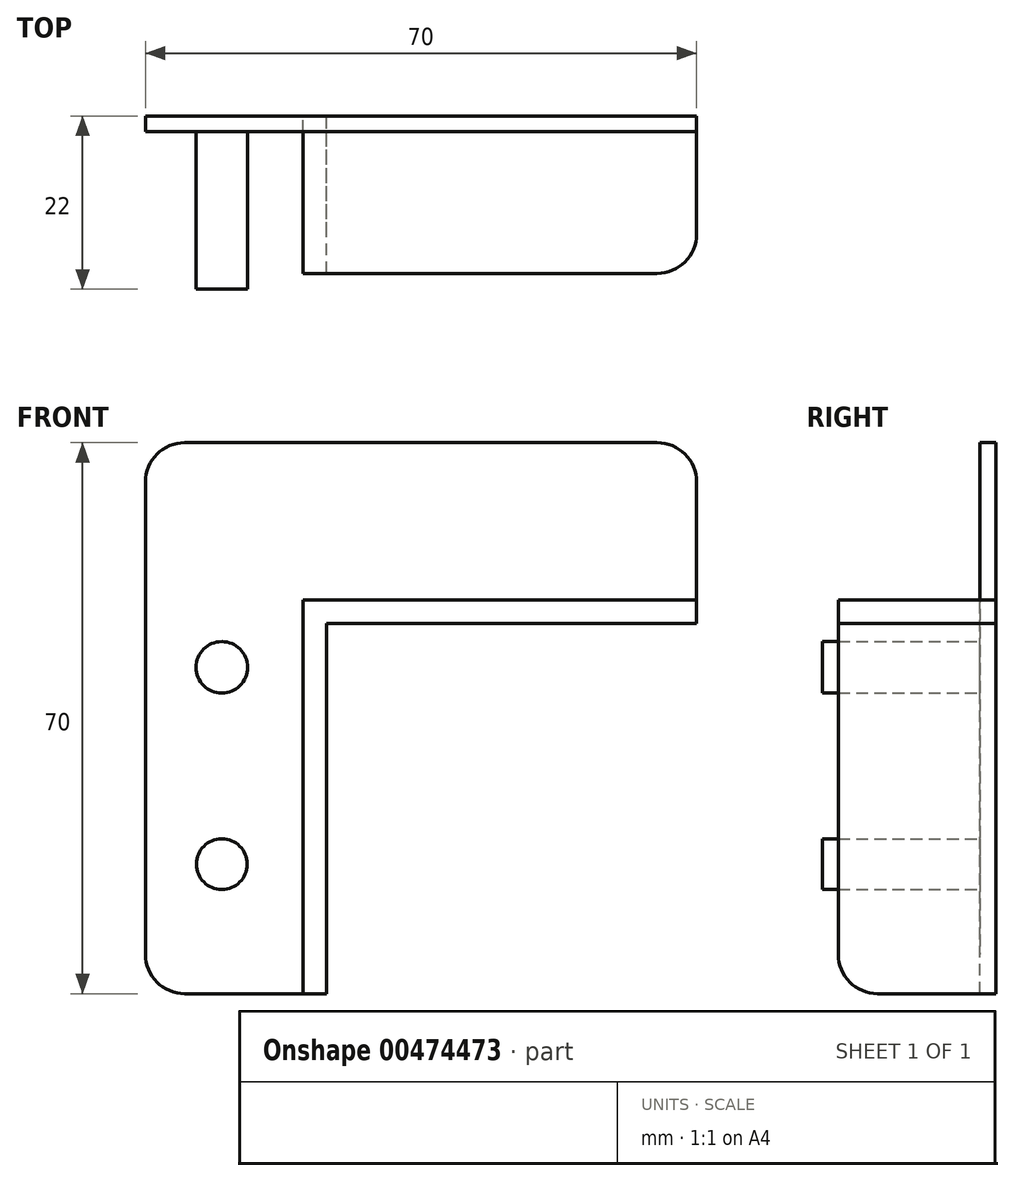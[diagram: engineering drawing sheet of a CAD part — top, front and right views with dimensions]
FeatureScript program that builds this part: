
annotation { "Feature Type Name" : "Feature", "Feature Type Description" : "" }
export const myFeature = defineFeature(function(context is Context, id is Id, definition is map)
    precondition{}
    {
        {
            var Q0;
            Q0=qCreatedBy(makeId("Front.planeOp"),FACE);
            var sketch = newSketch(context, id + "F0", { "sketchPlane" : qUnion([Q0])});
            skLineSegment(sketch, "E0.top", {"start": v(25, 25) * mm, "end": v(-25, 25) * mm});
            skLineSegment(sketch, "E0.right", {"start": v(-25, -25) * mm, "end": v(-25, 25) * mm});
            skPoint(sketch, "E0.middle", {"position": v(0, 0) * mm});
            skLineSegment(sketch, "E1.top", {"start": v(22, 22) * mm, "end": v(-22, 22) * mm});
            skLineSegment(sketch, "E1.right", {"start": v(-22, -22) * mm, "end": v(-22, 22) * mm});
            skLineSegment(sketch, "E2", {"start": v(22, 22) * mm, "end": v(25, 22) * mm});
            skLineSegment(sketch, "E3", {"start": v(-22, -22) * mm, "end": v(-22, -25) * mm});
            skLineSegment(sketch, "E4", {"start": v(-25, -25) * mm, "end": v(-22, -25) * mm});
            skLineSegment(sketch, "E5", {"start": v(25, 25) * mm, "end": v(25, 22) * mm});
            skSolve(sketch);
        }
        {
            var Q0;
            Q0 = qSketchRegion(id + "F0", true);
            extrude(context, id + "F1", {"entities" : qUnion([Q0]), "endBound" : BoundingType.SYMMETRIC, "depth" : 20 * mm});
        }
        {
            var Q0;
            Q0=makeQuery(id+"F1.opExtrude","CAP_FACE",FACE,{"disambiguationData":[OSD([sQuery(id+"F0.wireOp",EDGE,"E0.top"),sQuery(id+"F0.wireOp",EDGE,"E0.right"),sQuery(id+"F0.wireOp",EDGE,"E1.top"),sQuery(id+"F0.wireOp",EDGE,"E1.right"),sQuery(id+"F0.wireOp",EDGE,"E2"),sQuery(id+"F0.wireOp",EDGE,"E3"),sQuery(id+"F0.wireOp",EDGE,"E4"),sQuery(id+"F0.wireOp",EDGE,"E5")])],"isStart":true});
            var sketch = newSketch(context, id + "F2", { "sketchPlane" : qUnion([Q0])});
            skLineSegment(sketch, "E6.0", {"start": v(-25, 25) * mm, "end": v(25, 25) * mm});
            skLineSegment(sketch, "E7.0", {"start": v(25, -25) * mm, "end": v(25, 25) * mm});
            skLineSegment(sketch, "E8", {"start": v(-25, 25) * mm, "end": v(-25, 45) * mm});
            skLineSegment(sketch, "E9", {"start": v(-25, 45) * mm, "end": v(45, 45) * mm});
            skLineSegment(sketch, "E10", {"start": v(45, 45) * mm, "end": v(45, -25) * mm});
            skLineSegment(sketch, "E11", {"start": v(45, -25) * mm, "end": v(25, -25) * mm});
            skSolve(sketch);
        }
        {
            var Q0;
            Q0=makeQuery(id+"F2.imprint","IMPRINT",FACE,{"disambiguationData":[TD([[makeQuery(id+"F2.imprint","IMPRINT",EDGE,{"derivedFrom":sQuery(id+"F2.wireOp",EDGE,"E6.0")}),1.0]])]});
            extrude(context, id + "F3", {"entities" : qUnion([Q0]), "depth" : -2 * mm});
        }
        {
            var Q0;
            Q0=makeQuery(id+"F3.opExtrude","CAP_FACE",FACE,{"disambiguationData":[OSD([sQuery(id+"F2.wireOp",EDGE,"E6.0"),sQuery(id+"F2.wireOp",EDGE,"E7.0"),sQuery(id+"F2.wireOp",EDGE,"E8"),sQuery(id+"F2.wireOp",EDGE,"E9"),sQuery(id+"F2.wireOp",EDGE,"E10"),sQuery(id+"F2.wireOp",EDGE,"E11")])],"isStart":false});
            var sketch = newSketch(context, id + "F4", { "sketchPlane" : qUnion([Q0])});
            skCircle(sketch, "E12", {"center": v(-35.3, 16.45) * mm, "radius": 3.27 * mm});
            skCircle(sketch, "E13", {"center": v(-35.3, -8.55) * mm, "radius": 3.22 * mm});
            skLineSegment(sketch, "E14", {"start": v(-35.3, 16.45) * mm, "end": v(-35.3, -8.55) * mm, "construction": true});
            skSolve(sketch);
        }
        {
            var Q0;
            Q0 = qSketchRegion(id + "F4", true);
            extrude(context, id + "F5", {"entities" : qUnion([Q0]), "operationType" : NewBodyOperationType.ADD, "depth" : 20 * mm});
        }
        {
            var Q0;
            Q0=makeQuery(id+"F1.opExtrude","CAP_EDGE",EDGE,{"disambiguationData":[OSD([sQuery(id+"F0.wireOp",EDGE,"E5")])],"isStart":false});
            var Q1;
            Q1=makeQuery(id+"F1.opExtrude","CAP_EDGE",EDGE,{"disambiguationData":[OSD([sQuery(id+"F0.wireOp",EDGE,"E4")])],"isStart":false});
            var Q2;
            Q2=makeQuery(id+"F3.opExtrude","SWEPT_EDGE",EDGE,{"disambiguationData":[OSD([sQuery(id+"F2.wireOp",EDGE,"E8"),sQuery(id+"F2.wireOp",EDGE,"E9")])]});
            var Q3;
            Q3=makeQuery(id+"F3.opExtrude","SWEPT_EDGE",EDGE,{"disambiguationData":[OSD([sQuery(id+"F2.wireOp",EDGE,"E10"),sQuery(id+"F2.wireOp",EDGE,"E11")])]});
            var Q4;
            Q4=makeQuery(id+"F3.opExtrude","SWEPT_EDGE",EDGE,{"disambiguationData":[OSD([sQuery(id+"F2.wireOp",EDGE,"E9"),sQuery(id+"F2.wireOp",EDGE,"E10")])]});
            fillet(context, id + "F6", {"entities" : qUnion([Q0, Q1, Q2, Q3, Q4]), "radius" : 5 * mm, "tangentPropagation" : true, "allowEdgeOverflow" : false});
        }
        {
            var Q0;
            Q0=makeQuery(id+"F1.opExtrude","CAP_FACE",FACE,{"disambiguationData":[OSD([sQuery(id+"F0.wireOp",EDGE,"E0.top"),sQuery(id+"F0.wireOp",EDGE,"E0.right"),sQuery(id+"F0.wireOp",EDGE,"E1.top"),sQuery(id+"F0.wireOp",EDGE,"E1.right"),sQuery(id+"F0.wireOp",EDGE,"E2"),sQuery(id+"F0.wireOp",EDGE,"E3"),sQuery(id+"F0.wireOp",EDGE,"E4"),sQuery(id+"F0.wireOp",EDGE,"E5")])],"isStart":true});
            var sketch = newSketch(context, id + "F7", { "sketchPlane" : qUnion([Q0])});
            skCircle(sketch, "E15", {"center": v(18.38, 18.27) * mm, "radius": 3.62 * mm});
            skSolve(sketch);
        }
        {
            var Q0;
            Q0=sQuery(id+"F7.wireOp",EDGE,"E15");
            extrude(context, id + "F8", {"bodyType" : ToolBodyType.SURFACE, "surfaceEntities" : qUnion([Q0]), "depth" : -80 * mm});
        }
    });
